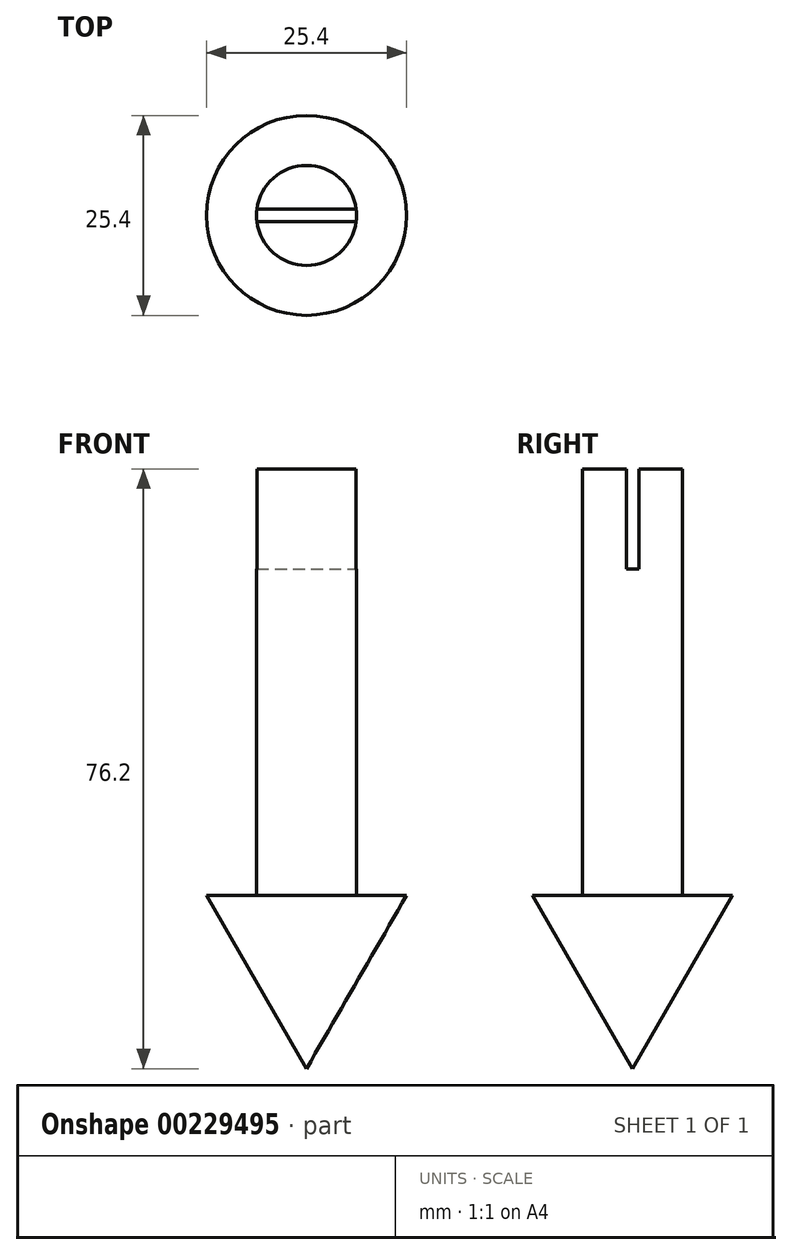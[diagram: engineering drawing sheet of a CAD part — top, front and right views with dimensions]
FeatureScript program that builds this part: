
annotation { "Feature Type Name" : "Feature", "Feature Type Description" : "" }
export const myFeature = defineFeature(function(context is Context, id is Id, definition is map)
    precondition{}
    {
        {
            var Q0;
            Q0=qCreatedBy(makeId("Right.planeOp"),FACE);
            var sketch = newSketch(context, id + "F0", { "sketchPlane" : qUnion([Q0])});
            skLineSegment(sketch, "E0", {"start": v(0, 76.2) * mm, "end": v(0, 0) * mm});
            skLineSegment(sketch, "E1", {"start": v(6.35, 76.2) * mm, "end": v(0, 76.2) * mm});
            skLineSegment(sketch, "E2", {"start": v(6.35, 22) * mm, "end": v(6.35, 76.2) * mm});
            skLineSegment(sketch, "E3", {"start": v(12.7, 22) * mm, "end": v(6.35, 22) * mm});
            skLineSegment(sketch, "E4", {"start": v(0, 0) * mm, "end": v(12.7, 22) * mm});
            skSolve(sketch);
        }
        {
            var Q0;
            Q0 = qSketchRegion(id + "F0", true);
            var Q1;
            Q1=sQuery(id+"F0.wireOp",EDGE,"E0");
            revolve(context, id + "F1", {"entities" : qUnion([Q0]), "axis" : qUnion([Q1]), "revolveType" : RevolveType.FULL});
        }
        {
            var Q0;
            Q0=makeQuery(id+"F1.opRevolve","SWEPT_FACE",FACE,{"disambiguationData":[OSD([sQuery(id+"F0.wireOp",EDGE,"E1")])]});
            var sketch = newSketch(context, id + "F2", { "sketchPlane" : qUnion([Q0])});
            skLineSegment(sketch, "E5.bottom", {"start": v(-12.7, -0.8) * mm, "end": v(12.7, -0.8) * mm});
            skLineSegment(sketch, "E5.top", {"start": v(-12.7, 0.8) * mm, "end": v(12.7, 0.8) * mm});
            skLineSegment(sketch, "E5.left", {"start": v(-12.7, -0.8) * mm, "end": v(-12.7, 0.8) * mm});
            skLineSegment(sketch, "E5.right", {"start": v(12.7, -0.8) * mm, "end": v(12.7, 0.8) * mm});
            skLineSegment(sketch, "E6", {"start": v(-12.7, 0.8) * mm, "end": v(12.7, -0.8) * mm, "construction": true});
            skSolve(sketch);
        }
        {
            var Q0;
            Q0 = qSketchRegion(id + "F2", true);
            extrude(context, id + "F3", {"entities" : qUnion([Q0]), "operationType" : NewBodyOperationType.REMOVE, "oppositeDirection" : true, "depth" : 12.7 * mm});
        }
    });
